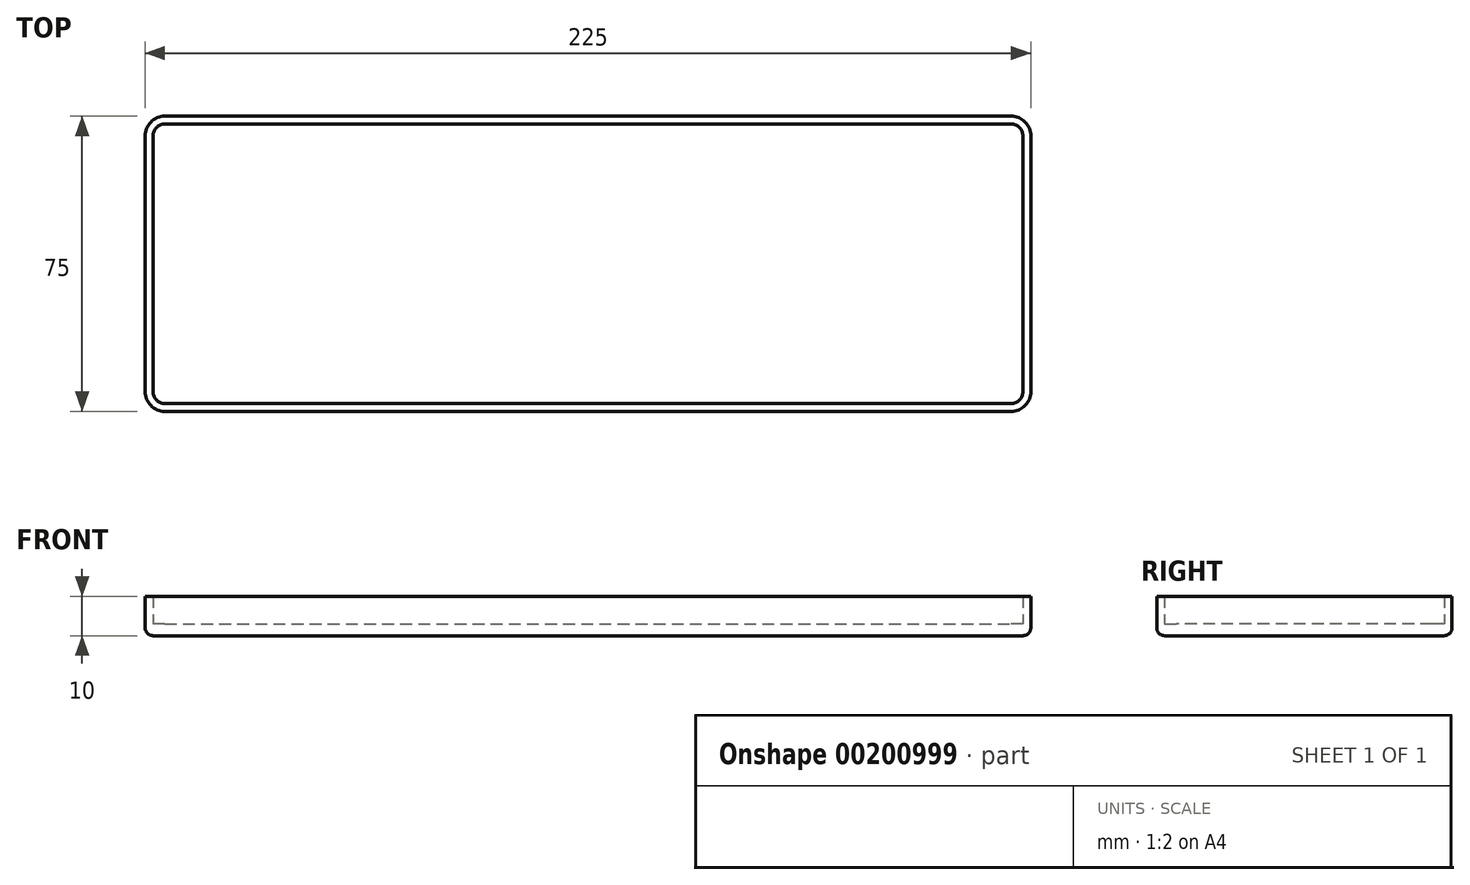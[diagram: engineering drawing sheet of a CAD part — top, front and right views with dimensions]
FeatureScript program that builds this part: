
annotation { "Feature Type Name" : "Feature", "Feature Type Description" : "" }
export const myFeature = defineFeature(function(context is Context, id is Id, definition is map)
    precondition{}
    {
        {
            var Q0;
            Q0=qCreatedBy(makeId("Top.planeOp"),FACE);
            var sketch = newSketch(context, id + "F0", { "sketchPlane" : qUnion([Q0])});
            skLineSegment(sketch, "E0.bottom", {"start": v(-41.61, 75) * mm, "end": v(173.39, 75) * mm});
            skLineSegment(sketch, "E0.top", {"start": v(-41.61, 0) * mm, "end": v(173.39, 0) * mm});
            skLineSegment(sketch, "E0.left", {"start": v(-46.61, 70) * mm, "end": v(-46.61, 5) * mm});
            skLineSegment(sketch, "E0.right", {"start": v(178.39, 70) * mm, "end": v(178.39, 5) * mm});
            skLineSegment(sketch, "E1.0", {"start": v(-41.61, 2) * mm, "end": v(173.39, 2) * mm});
            skLineSegment(sketch, "E1.1", {"start": v(-44.61, 70) * mm, "end": v(-44.61, 5) * mm});
            skLineSegment(sketch, "E1.2", {"start": v(-41.61, 73) * mm, "end": v(173.39, 73) * mm});
            skLineSegment(sketch, "E1.3", {"start": v(176.39, 70) * mm, "end": v(176.39, 5) * mm});
            skLineSegment(sketch, "E2", {"start": v(65.89, 73) * mm, "end": v(65.89, 2) * mm, "construction": true});
            skLineSegment(sketch, "E3", {"start": v(117.76, 37.5) * mm, "end": v(14.02, 37.5) * mm, "construction": true});
            skLineSegment(sketch, "E4", {"start": v(65.89, 37.5) * mm, "end": v(176.39, 37.5) * mm, "construction": true});
            skPoint(sketch, "E5.visualSharp", {"position": v(176.39, 73) * mm});
            skArc(sketch, "E5.filletArc", {"start": v(176.39, 70) * mm, "mid": v(175.5, 72.12) * mm, "end": v(173.39, 73) * mm});
            skPoint(sketch, "E6.visualSharp", {"position": v(-44.61, 73) * mm});
            skArc(sketch, "E6.filletArc", {"start": v(-41.61, 73) * mm, "mid": v(-43.73, 72.12) * mm, "end": v(-44.61, 70) * mm});
            skPoint(sketch, "E7.visualSharp", {"position": v(-44.61, 2) * mm});
            skArc(sketch, "E7.filletArc", {"start": v(-44.61, 5) * mm, "mid": v(-43.73, 2.88) * mm, "end": v(-41.61, 2) * mm});
            skPoint(sketch, "E8.visualSharp", {"position": v(176.39, 2) * mm});
            skArc(sketch, "E8.filletArc", {"start": v(173.39, 2) * mm, "mid": v(175.5, 2.88) * mm, "end": v(176.39, 5) * mm});
            skPoint(sketch, "E9.visualSharp", {"position": v(178.39, 0) * mm});
            skArc(sketch, "E9.filletArc", {"start": v(173.39, 0) * mm, "mid": v(176.92, 1.46) * mm, "end": v(178.39, 5) * mm});
            skPoint(sketch, "E10.visualSharp", {"position": v(178.39, 75) * mm});
            skArc(sketch, "E10.filletArc", {"start": v(178.39, 70) * mm, "mid": v(176.92, 73.54) * mm, "end": v(173.39, 75) * mm});
            skPoint(sketch, "E11.visualSharp", {"position": v(-46.61, 75) * mm});
            skArc(sketch, "E11.filletArc", {"start": v(-41.61, 75) * mm, "mid": v(-45.15, 73.54) * mm, "end": v(-46.61, 70) * mm});
            skPoint(sketch, "E12.visualSharp", {"position": v(-46.61, 0) * mm});
            skArc(sketch, "E12.filletArc", {"start": v(-46.61, 5) * mm, "mid": v(-45.15, 1.46) * mm, "end": v(-41.61, 0) * mm});
            skSolve(sketch);
        }
        {
            var Q0;
            Q0=makeQuery(id+"F0.imprint","IMPRINT",FACE,{"disambiguationData":[TD([[makeQuery(id+"F0.imprint","IMPRINT",EDGE,{"derivedFrom":sQuery(id+"F0.wireOp",EDGE,"E1.0")}),1.0]])]});
            var Q1;
            Q1=makeQuery(id+"F0.imprint","IMPRINT",FACE,{"disambiguationData":[TD([[makeQuery(id+"F0.imprint","IMPRINT",EDGE,{"derivedFrom":sQuery(id+"F0.wireOp",EDGE,"d484fe53-d81a-4631-bb7e-f7513ac6d46d.sketch_text.stroke-63")}),1.0]])]});
            var Q2;
            Q2=makeQuery(id+"F0.imprint","IMPRINT",FACE,{"disambiguationData":[TD([[makeQuery(id+"F0.imprint","IMPRINT",EDGE,{"derivedFrom":sQuery(id+"F0.wireOp",EDGE,"d484fe53-d81a-4631-bb7e-f7513ac6d46d.sketch_text.stroke-17")}),1.0]])]});
            extrude(context, id + "F1", {"entities" : qUnion([Q0, Q1, Q2]), "depth" : 3 * mm});
        }
        {
            var Q0;
            Q0=makeQuery(id+"F0.imprint","IMPRINT",FACE,{"disambiguationData":[TD([[makeQuery(id+"F0.imprint","IMPRINT",EDGE,{"derivedFrom":sQuery(id+"F0.wireOp",EDGE,"E0.bottom")}),-1.0]])]});
            extrude(context, id + "F2", {"entities" : qUnion([Q0]), "operationType" : NewBodyOperationType.ADD, "depth" : 10 * mm});
        }
        {
            var Q0;
            Q0=makeQuery(id+"F2.opExtrude","CAP_EDGE",EDGE,{"disambiguationData":[OSD([sQuery(id+"F0.wireOp",EDGE,"E0.bottom")])],"isStart":true});
            fillet(context, id + "F3", {"entities" : qUnion([Q0]), "radius" : 2 * mm, "tangentPropagation" : true, "allowEdgeOverflow" : false});
        }
    });
